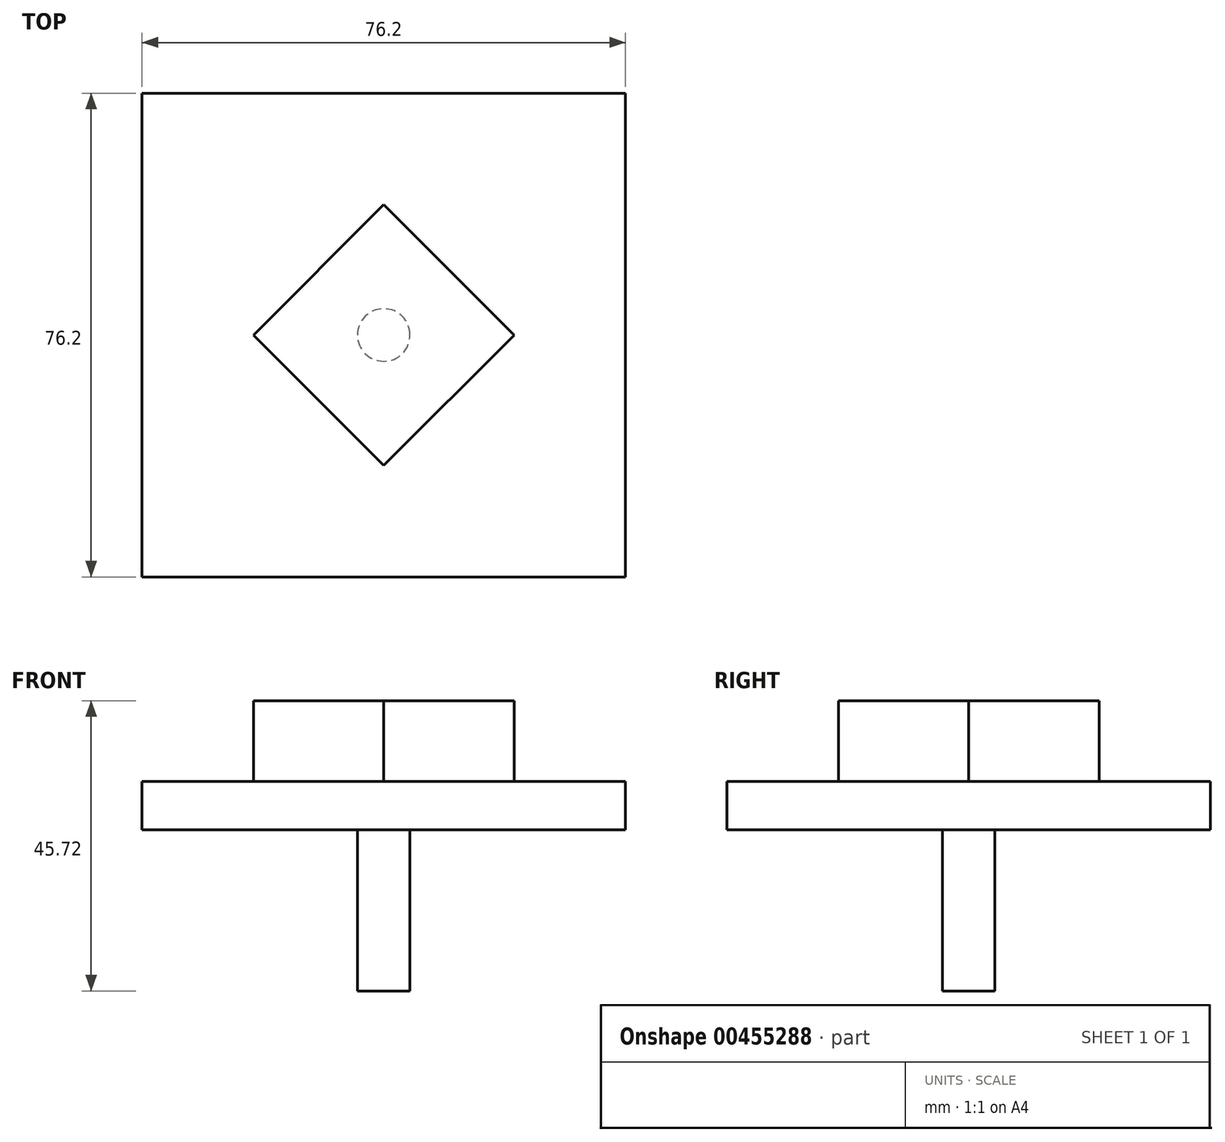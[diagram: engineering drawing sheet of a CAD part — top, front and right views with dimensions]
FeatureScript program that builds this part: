
annotation { "Feature Type Name" : "Feature", "Feature Type Description" : "" }
export const myFeature = defineFeature(function(context is Context, id is Id, definition is map)
    precondition{}
    {
        {
            var Q0;
            Q0=qCreatedBy(makeId("Top.planeOp"),FACE);
            var sketch = newSketch(context, id + "F0", { "sketchPlane" : qUnion([Q0])});
            skLineSegment(sketch, "E0.bottom", {"start": v(38.1, -38.1) * mm, "end": v(-38.1, -38.1) * mm});
            skLineSegment(sketch, "E0.top", {"start": v(38.1, 38.1) * mm, "end": v(-38.1, 38.1) * mm});
            skLineSegment(sketch, "E0.left", {"start": v(38.1, -38.1) * mm, "end": v(38.1, 38.1) * mm});
            skLineSegment(sketch, "E0.right", {"start": v(-38.1, -38.1) * mm, "end": v(-38.1, 38.1) * mm});
            skPoint(sketch, "E0.middle", {"position": v(0, 0) * mm});
            skSolve(sketch);
        }
        {
            var Q0;
            Q0 = qSketchRegion(id + "F0", true);
            extrude(context, id + "F1", {"entities" : qUnion([Q0]), "depth" : 7.62 * mm});
        }
        {
            var Q0;
            Q0=makeQuery(id+"F1.opExtrude","CAP_FACE",FACE,{"disambiguationData":[OSD([sQuery(id+"F0.wireOp",EDGE,"E0.bottom"),sQuery(id+"F0.wireOp",EDGE,"E0.top"),sQuery(id+"F0.wireOp",EDGE,"E0.left"),sQuery(id+"F0.wireOp",EDGE,"E0.right")])],"isStart":false});
            var sketch = newSketch(context, id + "F2", { "sketchPlane" : qUnion([Q0])});
            skCircle(sketch, "E1.cCircle", {"center": v(0, 0) * mm, "radius": 20.54 * mm, "construction": true});
            skLineSegment(sketch, "E1.0", {"start": v(0, -20.54) * mm, "end": v(-20.54, 0) * mm});
            skLineSegment(sketch, "E1.1", {"start": v(-20.54, 0) * mm, "end": v(0, 20.54) * mm});
            skLineSegment(sketch, "E1.2", {"start": v(0, 20.54) * mm, "end": v(20.54, 0) * mm});
            skLineSegment(sketch, "E1.3", {"start": v(20.54, 0) * mm, "end": v(0, -20.54) * mm});
            skSolve(sketch);
        }
        {
            var Q0;
            Q0 = qSketchRegion(id + "F2", true);
            extrude(context, id + "F3", {"entities" : qUnion([Q0]), "operationType" : NewBodyOperationType.ADD, "depth" : 12.7 * mm});
        }
        {
            var Q0;
            Q0=makeQuery(id+"F1.opExtrude","CAP_FACE",FACE,{"disambiguationData":[OSD([sQuery(id+"F0.wireOp",EDGE,"E0.bottom"),sQuery(id+"F0.wireOp",EDGE,"E0.top"),sQuery(id+"F0.wireOp",EDGE,"E0.left"),sQuery(id+"F0.wireOp",EDGE,"E0.right")])],"isStart":true});
            var sketch = newSketch(context, id + "F4", { "sketchPlane" : qUnion([Q0])});
            skCircle(sketch, "E2", {"center": v(0, 0) * mm, "radius": 4.14 * mm});
            skSolve(sketch);
        }
        {
            var Q0;
            Q0 = qSketchRegion(id + "F4", true);
            extrude(context, id + "F5", {"entities" : qUnion([Q0]), "operationType" : NewBodyOperationType.ADD, "depth" : 25.4 * mm});
        }
    });
